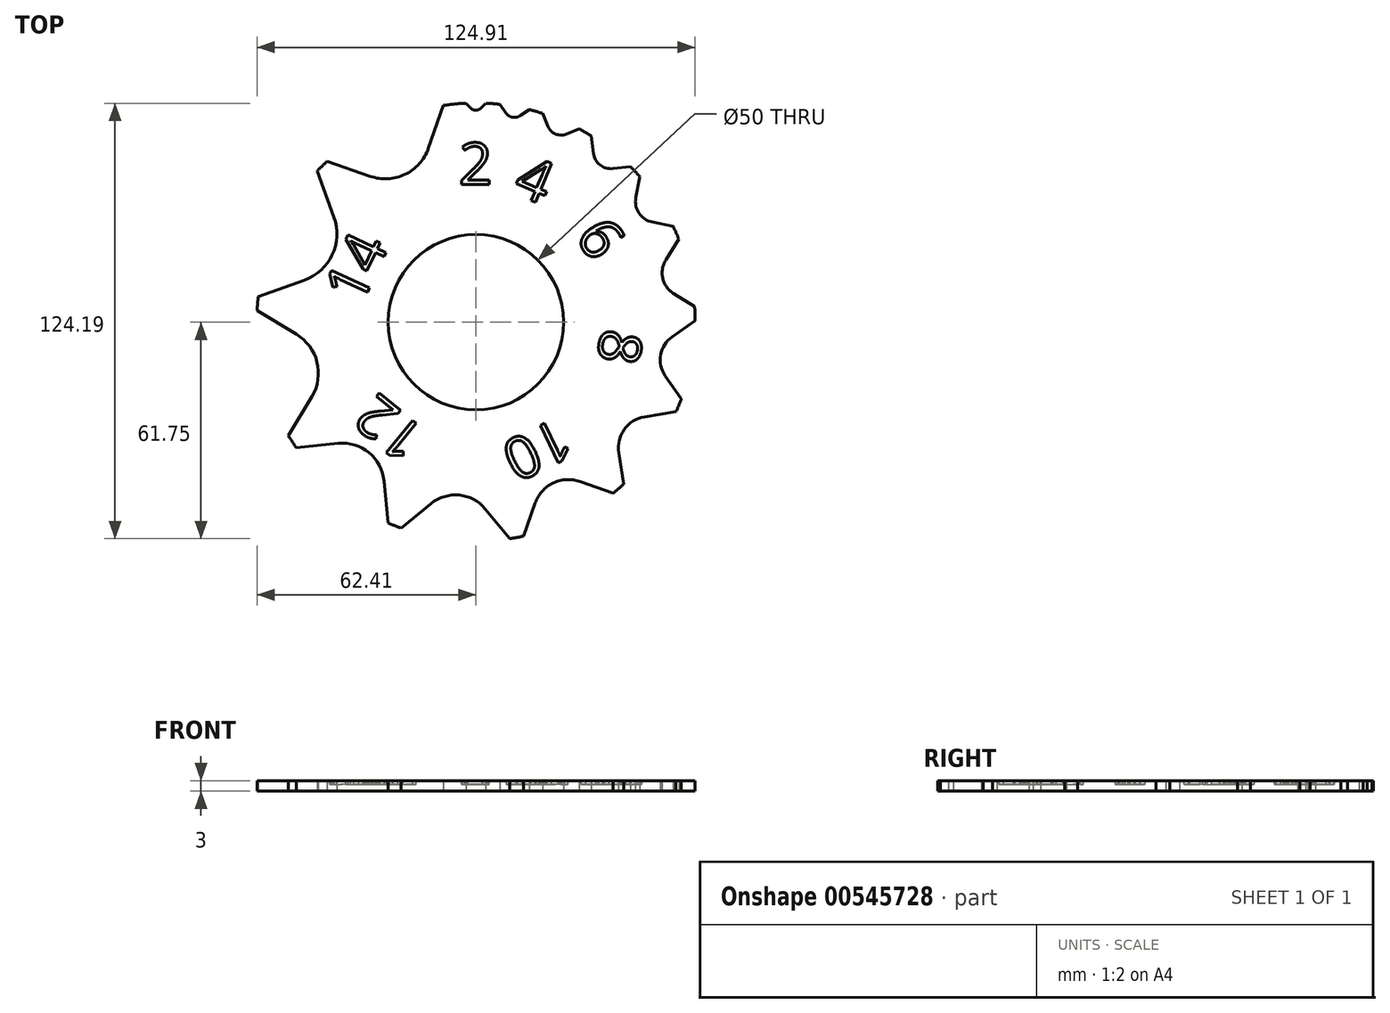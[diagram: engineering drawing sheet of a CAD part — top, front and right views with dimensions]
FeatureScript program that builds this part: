
annotation { "Feature Type Name" : "Feature", "Feature Type Description" : "" }
export const myFeature = defineFeature(function(context is Context, id is Id, definition is map)
    precondition{}
    {
        {
            assignVariable(context, id + "F0", {"name" : "thickness", "anyValue" : 3 * mm});
        }
        {
            var Q0;
            Q0=qCreatedBy(makeId("Top.planeOp"),FACE);
            var sketch = newSketch(context, id + "F1", { "sketchPlane" : qUnion([Q0])});
            skCircle(sketch, "E0", {"center": v(0, 0) * mm, "radius": 62.5 * mm});
            skSolve(sketch);
        }
        {
            var Q0;
            Q0 = qSketchRegion(id + "F1", true);
            extrude(context, id + "F2", {"entities" : qUnion([Q0]), "depth" : getVariable(context, 'thickness'), "offsetDistance" : 25 * mm});
        }
        {
            var Q0;
            Q0=qCreatedBy(makeId("Top.planeOp"),FACE);
            var sketch = newSketch(context, id + "F3", { "sketchPlane" : qUnion([Q0])});
            skArc(sketch, "E1", {"start": v(-1.41, 61.02) * mm, "mid": v(0, 60.44) * mm, "end": v(1.41, 61.02) * mm});
            skLineSegment(sketch, "E2", {"start": v(1.41, 61.02) * mm, "end": v(2.83, 62.44) * mm});
            skLineSegment(sketch, "E3", {"start": v(-1.41, 61.02) * mm, "end": v(-2.83, 62.44) * mm});
            skArc(sketch, "E4", {"start": v(8.53, 59.67) * mm, "mid": v(10.46, 58.43) * mm, "end": v(12.7, 58.92) * mm});
            skLineSegment(sketch, "E5", {"start": v(12.7, 58.92) * mm, "end": v(15.17, 60.63) * mm});
            skLineSegment(sketch, "E6", {"start": v(8.53, 59.67) * mm, "end": v(6.82, 62.13) * mm});
            skArc(sketch, "E7", {"start": v(20.52, 55.83) * mm, "mid": v(22.67, 53.65) * mm, "end": v(25.73, 53.63) * mm});
            skLineSegment(sketch, "E8", {"start": v(25.73, 53.63) * mm, "end": v(29.44, 55.13) * mm});
            skLineSegment(sketch, "E9", {"start": v(20.52, 55.83) * mm, "end": v(19.02, 59.54) * mm});
            skArc(sketch, "E10", {"start": v(33.5, 48.17) * mm, "mid": v(35.36, 44.83) * mm, "end": v(39.04, 43.8) * mm});
            skLineSegment(sketch, "E11", {"start": v(39.04, 43.8) * mm, "end": v(44, 44.38) * mm});
            skLineSegment(sketch, "E12", {"start": v(33.5, 48.17) * mm, "end": v(32.9, 53.14) * mm});
            skArc(sketch, "E13", {"start": v(45.59, 35.59) * mm, "mid": v(46.49, 31.08) * mm, "end": v(50.3, 28.53) * mm});
            skLineSegment(sketch, "E14", {"start": v(50.3, 28.53) * mm, "end": v(56.2, 27.37) * mm});
            skLineSegment(sketch, "E15", {"start": v(45.59, 35.59) * mm, "end": v(46.76, 41.47) * mm});
            skLineSegment(sketch, "E16", {"start": v(2.83, 62.44) * mm, "end": v(0, 65.26) * mm});
            skLineSegment(sketch, "E17", {"start": v(0, 65.26) * mm, "end": v(-2.83, 62.44) * mm});
            skLineSegment(sketch, "E18", {"start": v(15.17, 60.63) * mm, "end": v(11.74, 65.56) * mm});
            skLineSegment(sketch, "E19", {"start": v(11.74, 65.56) * mm, "end": v(6.82, 62.13) * mm});
            skLineSegment(sketch, "E20", {"start": v(29.44, 55.13) * mm, "end": v(26.43, 62.55) * mm});
            skLineSegment(sketch, "E21", {"start": v(26.43, 62.55) * mm, "end": v(19.02, 59.54) * mm});
            skLineSegment(sketch, "E22", {"start": v(44, 44.38) * mm, "end": v(42.84, 54.31) * mm});
            skLineSegment(sketch, "E23", {"start": v(42.84, 54.31) * mm, "end": v(32.9, 53.14) * mm});
            skLineSegment(sketch, "E24", {"start": v(56.2, 27.37) * mm, "end": v(58.53, 39.14) * mm});
            skLineSegment(sketch, "E25", {"start": v(58.53, 39.14) * mm, "end": v(46.76, 41.47) * mm});
            skArc(sketch, "E26", {"start": v(54.14, 17.77) * mm, "mid": v(53.27, 12.48) * mm, "end": v(56.4, 8.13) * mm});
            skLineSegment(sketch, "E27", {"start": v(56.4, 8.13) * mm, "end": v(62.34, 4.44) * mm});
            skLineSegment(sketch, "E28", {"start": v(54.14, 17.77) * mm, "end": v(57.83, 23.72) * mm});
            skLineSegment(sketch, "E29", {"start": v(62.34, 4.44) * mm, "end": v(69.72, 16.34) * mm});
            skLineSegment(sketch, "E30", {"start": v(69.72, 16.34) * mm, "end": v(57.83, 23.72) * mm});
            skArc(sketch, "E31", {"start": v(55.94, -4.14) * mm, "mid": v(52.65, -9.3) * mm, "end": v(53.97, -15.28) * mm});
            skLineSegment(sketch, "E32", {"start": v(53.97, -15.28) * mm, "end": v(58.56, -21.84) * mm});
            skLineSegment(sketch, "E33", {"start": v(55.94, -4.14) * mm, "end": v(62.5, 0.44) * mm});
            skLineSegment(sketch, "E34", {"start": v(58.56, -21.84) * mm, "end": v(71.67, -12.67) * mm});
            skLineSegment(sketch, "E35", {"start": v(71.67, -12.67) * mm, "end": v(62.5, 0.44) * mm});
            skArc(sketch, "E36", {"start": v(48.16, -26.97) * mm, "mid": v(42.3, -30.58) * mm, "end": v(40.7, -37.28) * mm});
            skLineSegment(sketch, "E37", {"start": v(40.7, -37.28) * mm, "end": v(42.13, -46.17) * mm});
            skLineSegment(sketch, "E38", {"start": v(48.16, -26.97) * mm, "end": v(57.04, -25.54) * mm});
            skLineSegment(sketch, "E39", {"start": v(42.13, -46.17) * mm, "end": v(59.9, -43.31) * mm});
            skLineSegment(sketch, "E40", {"start": v(59.9, -43.31) * mm, "end": v(57.04, -25.54) * mm});
            skArc(sketch, "E41", {"start": v(29.65, -45.45) * mm, "mid": v(22.01, -45.87) * mm, "end": v(16.9, -51.57) * mm});
            skLineSegment(sketch, "E42", {"start": v(16.9, -51.57) * mm, "end": v(13.59, -61) * mm});
            skLineSegment(sketch, "E43", {"start": v(29.65, -45.45) * mm, "end": v(39.09, -48.77) * mm});
            skLineSegment(sketch, "E44", {"start": v(13.59, -61) * mm, "end": v(32.45, -67.64) * mm});
            skLineSegment(sketch, "E45", {"start": v(32.45, -67.64) * mm, "end": v(39.09, -48.77) * mm});
            skArc(sketch, "E46", {"start": v(2.66, -53.26) * mm, "mid": v(-4.77, -49.3) * mm, "end": v(-12.82, -51.76) * mm});
            skLineSegment(sketch, "E47", {"start": v(-12.82, -51.76) * mm, "end": v(-21.31, -58.75) * mm});
            skLineSegment(sketch, "E48", {"start": v(2.66, -53.26) * mm, "end": v(9.66, -61.75) * mm});
            skLineSegment(sketch, "E49", {"start": v(-21.31, -58.75) * mm, "end": v(-7.33, -75.74) * mm});
            skLineSegment(sketch, "E50", {"start": v(-7.33, -75.74) * mm, "end": v(9.66, -61.75) * mm});
            skArc(sketch, "E51", {"start": v(-26.2, -45.33) * mm, "mid": v(-30.54, -37.23) * mm, "end": v(-39.33, -34.57) * mm});
            skLineSegment(sketch, "E52", {"start": v(-39.33, -34.57) * mm, "end": v(-51.27, -35.75) * mm});
            skLineSegment(sketch, "E53", {"start": v(-26.2, -45.33) * mm, "end": v(-25.03, -57.27) * mm});
            skLineSegment(sketch, "E54", {"start": v(-51.27, -35.75) * mm, "end": v(-48.91, -59.63) * mm});
            skLineSegment(sketch, "E55", {"start": v(-48.91, -59.63) * mm, "end": v(-25.03, -57.27) * mm});
            skArc(sketch, "E56", {"start": v(-46.78, -21.24) * mm, "mid": v(-45.32, -11.4) * mm, "end": v(-51.26, -3.4) * mm});
            skLineSegment(sketch, "E57", {"start": v(-51.26, -3.4) * mm, "end": v(-62.41, 3.27) * mm});
            skLineSegment(sketch, "E58", {"start": v(-46.78, -21.24) * mm, "end": v(-53.45, -32.4) * mm});
            skLineSegment(sketch, "E59", {"start": v(-62.41, 3.27) * mm, "end": v(-75.76, -19.04) * mm});
            skLineSegment(sketch, "E60", {"start": v(-75.76, -19.04) * mm, "end": v(-53.45, -32.4) * mm});
            skArc(sketch, "E61", {"start": v(-48.91, 12.01) * mm, "mid": v(-41, 19.23) * mm, "end": v(-40.5, 29.94) * mm});
            skLineSegment(sketch, "E62", {"start": v(-40.5, 29.94) * mm, "end": v(-45.26, 43.1) * mm});
            skLineSegment(sketch, "E63", {"start": v(-48.91, 12.01) * mm, "end": v(-62.08, 7.25) * mm});
            skLineSegment(sketch, "E64", {"start": v(-45.26, 43.1) * mm, "end": v(-71.6, 33.59) * mm});
            skLineSegment(sketch, "E65", {"start": v(-71.6, 33.59) * mm, "end": v(-62.08, 7.25) * mm});
            skArc(sketch, "E66", {"start": v(-30.15, 41.6) * mm, "mid": v(-20.21, 42.14) * mm, "end": v(-13.57, 49.55) * mm});
            skLineSegment(sketch, "E67", {"start": v(-13.57, 49.55) * mm, "end": v(-9.26, 61.81) * mm});
            skLineSegment(sketch, "E68", {"start": v(-30.15, 41.6) * mm, "end": v(-42.4, 45.9) * mm});
            skLineSegment(sketch, "E69", {"start": v(-9.26, 61.81) * mm, "end": v(-33.78, 70.44) * mm});
            skLineSegment(sketch, "E70", {"start": v(-33.78, 70.44) * mm, "end": v(-42.4, 45.9) * mm});
            skSolve(sketch);
        }
        {
            var Q0;
            Q0 = qSketchRegion(id + "F3", true);
            extrude(context, id + "F4", {"entities" : qUnion([Q0]), "operationType" : NewBodyOperationType.REMOVE, "endBound" : BoundingType.THROUGH_ALL, "depth" : 25 * mm, "offsetDistance" : 25 * mm});
        }
        {
            var Q0;
            Q0=sQuery(id+"F1.wireOp",VERTEX,"E0.center");
            var Q1;
            Q1=makeQuery(id+"F2.opExtrude","SWEPT_BODY",BODY,{"disambiguationData":[OSD([sQuery(id+"F1.wireOp",EDGE,"E0")])]});
            hole(context, id + "F5", {"style" : HoleStyle.SIMPLE, "endStyle" : HoleEndStyle.THROUGH, "oppositeDirection" : true, "holeDiameter" : 50 * mm, "isTappedThrough" : true, "tappedDepth" : 12.7 * mm, "tapClearance" : 3, "startFromSketch" : true, "locations" : qUnion([Q0]), "scope" : qUnion([Q1])});
        }
        {
            var Q0;
            Q0=makeQuery(id+"F2.opExtrude","CAP_FACE",FACE,{"disambiguationData":[OSD([sQuery(id+"F1.wireOp",EDGE,"E0")])],"isStart":false});
            var sketch = newSketch(context, id + "F6", { "sketchPlane" : qUnion([Q0])});
            skText(sketch, "E71", { "text": "2", "fontName": "OpenSans-Regular.ttf"});
            skText(sketch, "E72", { "text": "4", "fontName": "OpenSans-Regular.ttf"});
            skLineSegment(sketch, "E73", {"start": v(18.54, 43.87) * mm, "end": v(22.67, 53.65) * mm});
            skLineSegment(sketch, "E74", {"start": v(9.73, 23.03) * mm, "end": v(13.87, 32.81) * mm});
            skLineSegment(sketch, "E75", {"start": v(0, 60.44) * mm, "end": v(0, 48.72) * mm});
            skLineSegment(sketch, "E76", {"start": v(0, 36.72) * mm, "end": v(0, 25) * mm});
            skText(sketch, "E77", { "text": "6", "fontName": "OpenSans-Regular.ttf"});
            skLineSegment(sketch, "E78", {"start": v(28.65, 19.16) * mm, "end": v(20.78, 13.9) * mm});
            skLineSegment(sketch, "E79", {"start": v(38.62, 25.83) * mm, "end": v(46.49, 31.08) * mm});
            skText(sketch, "E80", { "text": "8", "fontName": "OpenSans-Regular.ttf"});
            skLineSegment(sketch, "E81", {"start": v(44.54, -7.87) * mm, "end": v(52.65, -9.3) * mm});
            skLineSegment(sketch, "E82", {"start": v(32.73, -5.78) * mm, "end": v(24.62, -4.35) * mm});
            skText(sketch, "E83", { "text": "10", "fontName": "OpenSans-Regular.ttf"});
            skLineSegment(sketch, "E84", {"start": v(22.01, -45.87) * mm, "end": v(19, -39.62) * mm});
            skLineSegment(sketch, "E85", {"start": v(13.82, -28.8) * mm, "end": v(10.82, -22.54) * mm});
            skText(sketch, "E86", { "text": "12", "fontName": "OpenSans-Regular.ttf"});
            skLineSegment(sketch, "E87", {"start": v(-19.4, -23.64) * mm, "end": v(-15.85, -19.33) * mm});
            skLineSegment(sketch, "E88", {"start": v(-30.54, -37.23) * mm, "end": v(-27, -32.92) * mm});
            skText(sketch, "E89", { "text": "14", "fontName": "OpenSans-Regular.ttf"});
            skLineSegment(sketch, "E90", {"start": v(-26.38, 12.38) * mm, "end": v(-22.63, 10.62) * mm});
            skLineSegment(sketch, "E91", {"start": v(-37.25, 17.47) * mm, "end": v(-41, 19.23) * mm});
            const initialGuessF6  = {"E71": [-0.00486, 0.03922, 1, 0, 0.012], "E72": [0.0101, 0.03712, 0.92114, -0.38923, 0.012], "E77": [0.028, 0.02462, 0.55586, -0.83127, 0.012], "E80": [0.03604, -0.00142, -0.17406, -0.98473, 0.012], "E83": [0.0236, -0.02687, -0.90158, -0.43261, 0.012], "E86": [-0.01354, -0.03168, -0.77318, 0.63419, 0.012], "E89": [-0.03285, 0.00447, 0.42472, 0.90533, 0.012]};
            skSetInitialGuess(sketch, initialGuessF6);
            skSolve(sketch);
        }
        {
            var Q0;
            Q0 = qSketchRegion(id + "F6", true);
            extrude(context, id + "F7", {"entities" : qUnion([Q0]), "operationType" : NewBodyOperationType.REMOVE, "oppositeDirection" : true, "depth" : 1 * mm, "offsetDistance" : 25 * mm});
        }
    });
